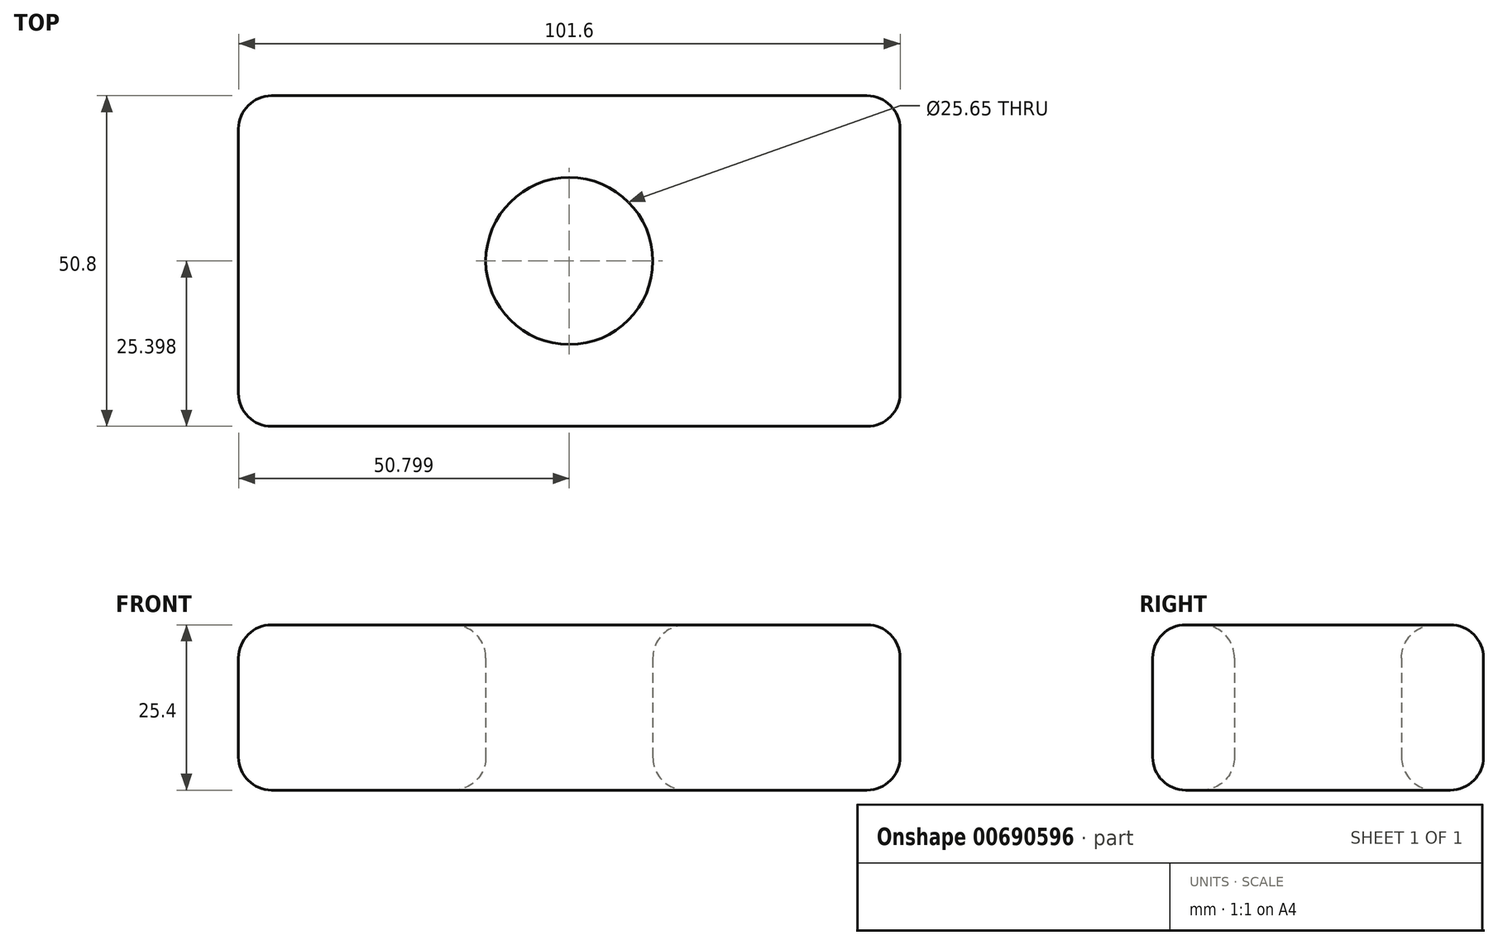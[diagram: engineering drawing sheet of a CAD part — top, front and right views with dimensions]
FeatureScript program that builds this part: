
annotation { "Feature Type Name" : "Feature", "Feature Type Description" : "" }
export const myFeature = defineFeature(function(context is Context, id is Id, definition is map)
    precondition{}
    {
        {
            var Q0;
            Q0=qCreatedBy(makeId("Top.planeOp"),FACE);
            var sketch = newSketch(context, id + "F0", { "sketchPlane" : qUnion([Q0])});
            skLineSegment(sketch, "E0.bottom", {"start": v(-46.46, -22.74) * mm, "end": v(55.14, -22.74) * mm});
            skLineSegment(sketch, "E0.top", {"start": v(-46.46, 28.06) * mm, "end": v(55.14, 28.06) * mm});
            skLineSegment(sketch, "E0.left", {"start": v(-46.46, -22.74) * mm, "end": v(-46.46, 28.06) * mm});
            skLineSegment(sketch, "E0.right", {"start": v(55.14, -22.74) * mm, "end": v(55.14, 28.06) * mm});
            skCircle(sketch, "E1", {"center": v(4.34, 2.66) * mm, "radius": 12.83 * mm});
            skSolve(sketch);
        }
        {
            var Q0;
            Q0=makeQuery(id+"F0.imprint","IMPRINT",FACE,{"disambiguationData":[TD([[makeQuery(id+"F0.imprint","IMPRINT",EDGE,{"derivedFrom":sQuery(id+"F0.wireOp",EDGE,"E0.bottom")}),1.0]])]});
            extrude(context, id + "F1", {"entities" : qUnion([Q0]), "depth" : 25.4 * mm, "offsetDistance" : 25.4 * mm});
        }
        {
            var Q0;
            Q0=makeQuery(id+"F1.opExtrude","CAP_FACE",FACE,{"disambiguationData":[OSD([sQuery(id+"F0.wireOp",EDGE,"E0.bottom"),sQuery(id+"F0.wireOp",EDGE,"E0.top"),sQuery(id+"F0.wireOp",EDGE,"E0.left"),sQuery(id+"F0.wireOp",EDGE,"E0.right")])],"isStart":false});
            var Q1;
            Q1=makeQuery(id+"F1.opExtrude","CAP_FACE",FACE,{"disambiguationData":[OSD([sQuery(id+"F0.wireOp",EDGE,"E0.bottom"),sQuery(id+"F0.wireOp",EDGE,"E0.top"),sQuery(id+"F0.wireOp",EDGE,"E0.left"),sQuery(id+"F0.wireOp",EDGE,"E0.right")])],"isStart":true});
            var Q2;
            Q2=makeQuery(id+"F1.opExtrude","SWEPT_FACE",FACE,{"disambiguationData":[OSD([sQuery(id+"F0.wireOp",EDGE,"E0.bottom")])]});
            var Q3;
            Q3=makeQuery(id+"F1.opExtrude","SWEPT_FACE",FACE,{"disambiguationData":[OSD([sQuery(id+"F0.wireOp",EDGE,"E0.top")])]});
            fillet(context, id + "F2", {"entities" : qUnion([Q0, Q1, Q2, Q3]), "radius" : 5.08 * mm, "tangentPropagation" : true, "allowEdgeOverflow" : false});
        }
    });
